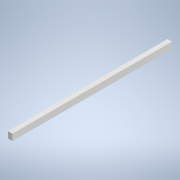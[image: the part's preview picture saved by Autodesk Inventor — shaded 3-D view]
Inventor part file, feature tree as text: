
AUTODESK INVENTOR PART (.ipt)
format: ipt  version: 2021 (Build 250183000, 183)  size: 119,808 bytes
history: native  units: mm
features: extrude x3, sketch x3, fillet x1
ambient origin geometry x8: Origin, YZ Plane, XZ Plane, XY Plane, X Axis, Y Axis, Z Axis, Center Point
bodies: Solid1 (feature_tree)
feature tree (7):
  extrude  "Extrusion1"  Depth=10.0mm
  extrude  "Extrusion2"  Depth=5.0mm
  fillet  "Fillet1"  Radius=65.0mm
  extrude  "Extrusion3"  Depth=2.0mm
  sketch  "Sketch1"  dims[d0=7.0mm d1=10.0mm]
  sketch  "Sketch2"  dims[d2=250.0mm d3=0.0mm d4=5.0mm d5=65.0mm]
  sketch  "Sketch3"  dims[d6=100.0mm d7=0.0mm d8=2.0mm d9=4.0mm d10=0.0mm d11=0.0mm]
